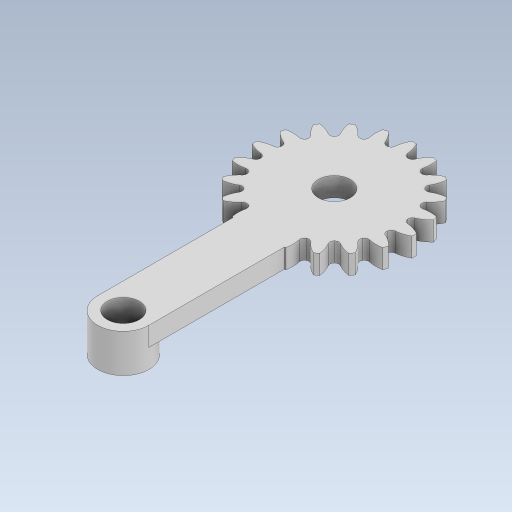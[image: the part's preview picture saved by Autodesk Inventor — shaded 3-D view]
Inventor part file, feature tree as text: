
AUTODESK INVENTOR PART (.ipt)
format: ipt  version: 2023.5 (Build 275446000, 446)  size: 526,336 bytes
history: native  units: in
note: dims shown in document units (in); Inventor stores cm internally (conversion verified against a paired STEP export)
features: extrude x4, sketch x2, fillet x1, pattern_circular x1, plane x1
ambient origin geometry x8: Origin, YZ Plane, XZ Plane, XY Plane, X Axis, Y Axis, Z Axis, Center Point
bodies: Solid1 (feature_tree)
feature tree (9):
  sketch  "Sketch1"  dims[d0=0.7874in d1=0.9843in]
  extrude  "Extrusion1"  Depth=0.9843in
  extrude  "Extrusion3"  Depth=0.1181in
  fillet  "Fillet1"  Radius=0.0276in
  pattern_circular  "Circular Pattern1"  [2 undecoded]
  plane  "Work Plane1"
  sketch  "Sketch2"  dims[d2=0.9055in d3=0.0787in d4=0.0276in d5=0.1181in d6=0.0in d9=0.1181in d10=0.0in d11=0.0276in d12=7.874in d13=360.0deg d15=0.1969in d16=0.315in d17=1.2992in d18=0.2756in d19=0.1969in d20=0.1181in d21=0.0in d22=0.1772in d23=0.0in d24=0.0197in d25=0.0344in]
  extrude  "Extrusion4"  Depth=0.1181in TaperAngle=0.0deg
  extrude  "Extrusion5"  Depth=0.0276in
note: 2 required parameter values undecoded (feature->parameter linkage not recoverable at this tier; creation-order binding heuristic only, values carry confidence <= 0.55)
